# Revit family: Hekatron_Raumlufttechnik_LRS 230 V DIBt_DE_22.01
name_source: partatom
category: Brandmelder
revit_build: Autodesk Revit 2018 (Build: 20190510_1515(x64)
units: mm (PartAtom-declared; Revit-internal decimal feet)

## family parameters
Basisbauteil = Fläche
Beim Laden mit Abzugskörper schneiden = Nein
Bemaßung runder Anschluss = Durchmesser verwenden
Beschriftungsausrichtung beibehalten = Ja
Gemeinsam genutzt = Nein
OmniClass-Nummer = 23.85.30.21
OmniClass-Titel = Environmental Detection/Registration
Raumberechnungspunkt = Nein
Teiletyp = Normal

## types (1)
- LRS 230 V DIBt
    Bauartgenehmigungen = Z-78.6-177
    Beschreibung = Lüftungs-Rauchschalter-System zur Rauchüberwachung von Lüftungsleitungen, DIBt-konforme Ansteuerung von Brand- und Rauchschutzklappen und Steuerung von weiteren Anwendungen wie Lüftungsventilatoren.
    Betriebsspannung = 230 V AC
    Breite (mm) = 520.0
    Farbe = blau
    Funktionsprinzip = optisch
    Hersteller = Hekatron
    Höhe (mm) = 441.0
    Kabeleinführung = seitlich
    Link zu Ausschreibungstext = https://www.meinhplus.de
    Link zu Produktinformation = https://www.hekatron-planungstools.de
    Link zu ausschreiben.de = http://www.ausschreiben.de
    Material = PC / eloxiertes Alurohr
    Modell = LRS 230 V DIBt
    Montageart = am Kanal
    Nettogewicht (g) = 2100.0
    Schutzart = IP 30
    Tiefe (mm) = 135.0
    Typenkommentare = Lüftungs Rauchschalter Ausführung 230 V DIBt
    UB A&S Artikel Nummer = 31-5000007-01-01
    URL = https://www.hekatron-brandschutz.de
    VdS-Anerkennung = G 207085
    Version des BIM Objektes = 22.01
    Vorgabe-Ansicht = 1200 mm
    Zulässige Luftgeschwindigkeit = 1 bis 20 m/s
    Zulässige Umgebungstemperatur = +5 °C bis +40 °C

## geometry (parser evidence)
native form markers: Sweep x2
no freeform markers — native parametric forms only
